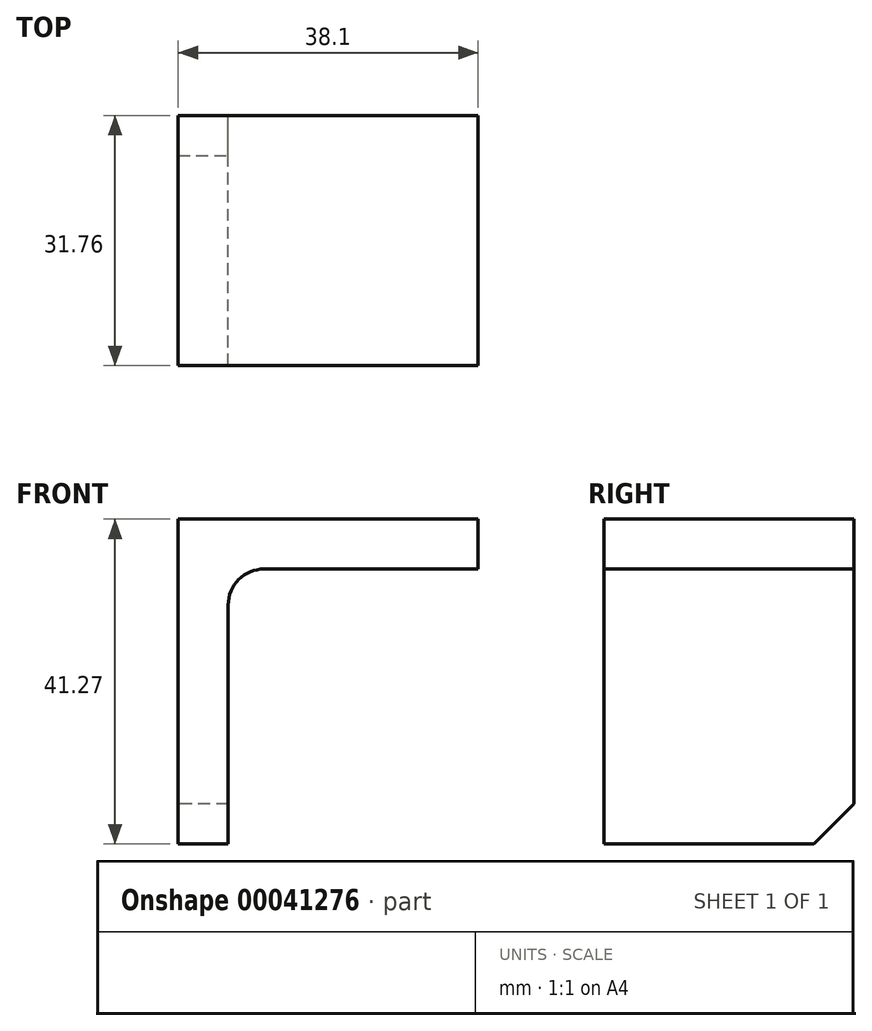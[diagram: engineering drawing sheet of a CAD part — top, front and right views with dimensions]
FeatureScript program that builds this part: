
annotation { "Feature Type Name" : "Feature", "Feature Type Description" : "" }
export const myFeature = defineFeature(function(context is Context, id is Id, definition is map)
    precondition{}
    {
        {
            var Q0;
            Q0=qCreatedBy(makeId("Front.planeOp"),FACE);
            var sketch = newSketch(context, id + "F0", { "sketchPlane" : qUnion([Q0])});
            skLineSegment(sketch, "E0", {"start": v(0, 0) * mm, "end": v(0, 41.28) * mm});
            skLineSegment(sketch, "E1", {"start": v(0, 41.28) * mm, "end": v(38.1, 41.28) * mm});
            skLineSegment(sketch, "E2", {"start": v(38.1, 41.28) * mm, "end": v(38.1, 34.93) * mm});
            skLineSegment(sketch, "E3", {"start": v(38.1, 34.93) * mm, "end": v(6.35, 34.93) * mm});
            skLineSegment(sketch, "E4", {"start": v(6.35, 34.93) * mm, "end": v(6.35, 0) * mm});
            skLineSegment(sketch, "E5", {"start": v(6.35, 0) * mm, "end": v(0, 0) * mm});
            skSolve(sketch);
        }
        {
            var Q0;
            Q0=makeQuery(id+"F0.imprint","IMPRINT",FACE,{"disambiguationData":[TD([[makeQuery(id+"F0.imprint","IMPRINT",EDGE,{"derivedFrom":sQuery(id+"F0.wireOp",EDGE,"E0")}),-1.0]])]});
            extrude(context, id + "F1", {"entities" : qUnion([Q0]), "depth" : 31.75 * mm, "symmetric" : true});
        }
        {
            var Q0;
            Q0=makeQuery(id+"F1.opExtrude","SWEPT_EDGE",EDGE,{"disambiguationData":[OSD([sQuery(id+"F0.wireOp",EDGE,"E3"),sQuery(id+"F0.wireOp",EDGE,"E4")])]});
            fillet(context, id + "F2", {"entities" : qUnion([Q0]), "radius" : 4.57 * mm, "tangentPropagation" : true, "allowEdgeOverflow" : false});
        }
        {
            var Q0;
            Q0=makeQuery(id+"F1.opExtrude","CAP_EDGE",EDGE,{"disambiguationData":[OSD([sQuery(id+"F0.wireOp",EDGE,"E5")])],"isStart":true});
            chamfer(context, id + "F3", {"entities" : qUnion([Q0]), "width" : 5.08 * mm, "tangentPropagation" : true});
        }
    });
